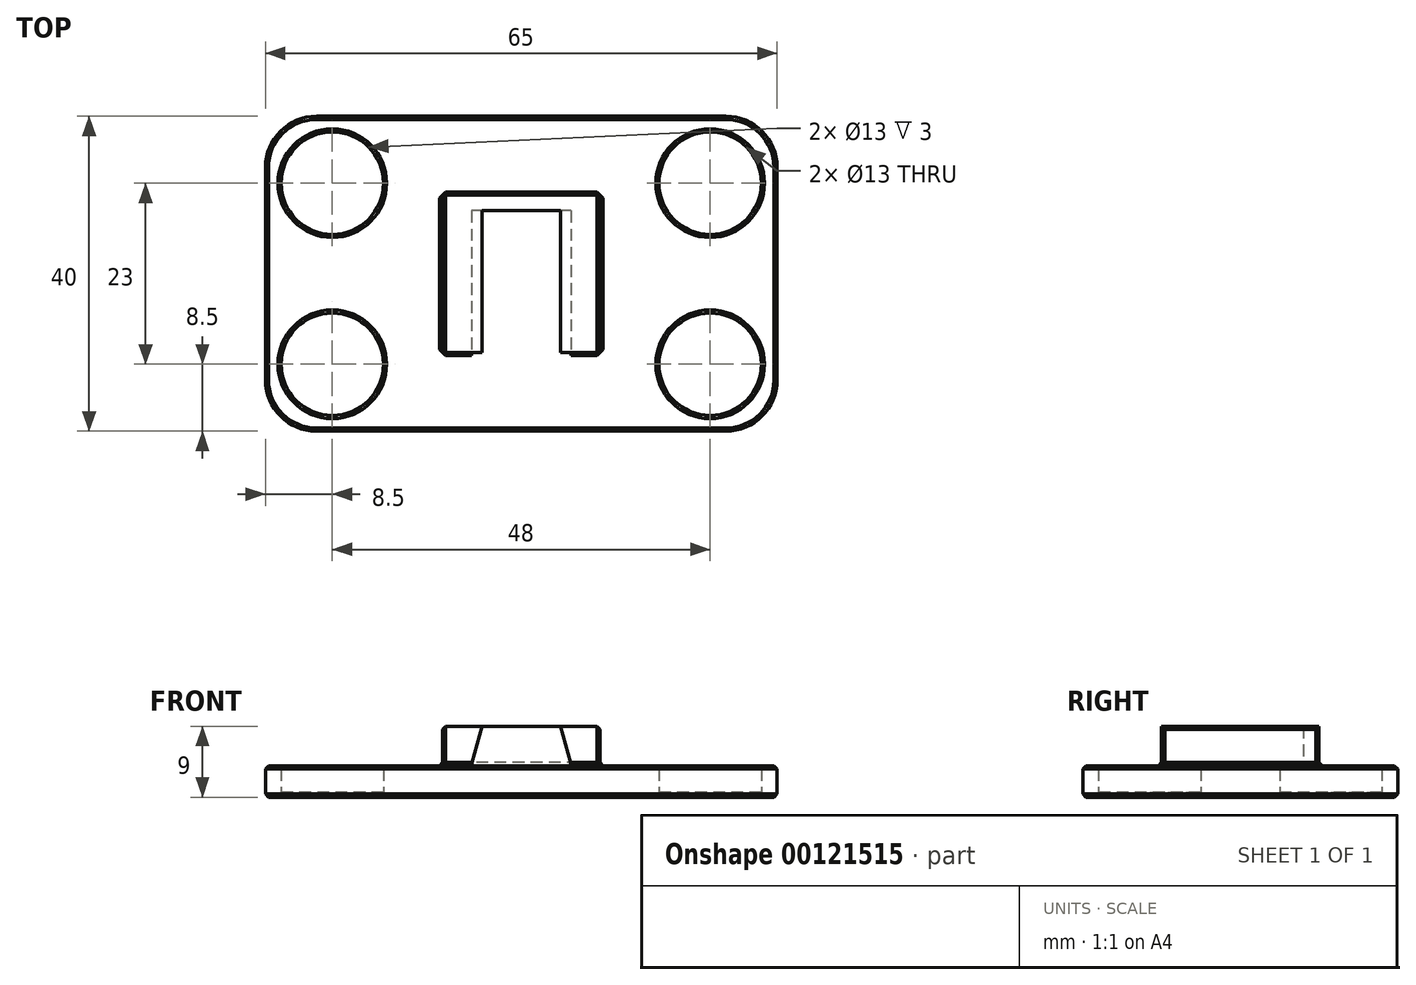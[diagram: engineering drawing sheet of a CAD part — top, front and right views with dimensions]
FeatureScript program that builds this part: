
annotation { "Feature Type Name" : "Feature", "Feature Type Description" : "" }
export const myFeature = defineFeature(function(context is Context, id is Id, definition is map)
    precondition{}
    {
        {
            assignVariable(context, id + "F0", {"name" : "PrintOffset", "anyValue" : 0.4});
        }
        {
            assignVariable(context, id + "F1", {"name" : "DovetailBackstopDepth", "anyValue" : 2});
        }
        {
            assignVariable(context, id + "F2", {"name" : "DovetailDepth", "anyValue" : 20});
        }
        {
            assignVariable(context, id + "F3", {"name" : "DovetailHeight", "anyValue" : 5});
        }
        {
            assignVariable(context, id + "F4", {"name" : "MagnetDiameter", "anyValue" : 13});
        }
        {
            assignVariable(context, id + "F5", {"name" : "WallThickness", "anyValue" : 4});
        }
        {
            var Q0;
            Q0=qCreatedBy(makeId("Top.planeOp"),FACE);
            var sketch = newSketch(context, id + "F6", { "sketchPlane" : qUnion([Q0])});
            skLineSegment(sketch, "E0", {"start": v(0, 0) * mm, "end": v(65, 0) * mm});
            skLineSegment(sketch, "E1", {"start": v(65, 0) * mm, "end": v(65, 40) * mm});
            skLineSegment(sketch, "E2", {"start": v(65, 40) * mm, "end": v(0, 40) * mm});
            skLineSegment(sketch, "E3", {"start": v(0, 40) * mm, "end": v(0, 0) * mm});
            skLineSegment(sketch, "E4", {"start": v(32.5, 40) * mm, "end": v(32.5, 0) * mm, "construction": true});
            skLineSegment(sketch, "E5", {"start": v(0, 20) * mm, "end": v(65, 20) * mm, "construction": true});
            skCircle(sketch, "E6", {"center": v(8.5, 31.5) * mm, "radius": 6.5 * mm});
            skCircle(sketch, "E7.MirrorC", {"center": v(56.5, 31.5) * mm, "radius": 6.5 * mm});
            skCircle(sketch, "E8.MirrorC", {"center": v(56.5, 8.5) * mm, "radius": 6.5 * mm});
            skCircle(sketch, "E9.MirrorC", {"center": v(8.5, 8.5) * mm, "radius": 6.5 * mm});
            skLineSegment(sketch, "E10.bottom", {"start": v(42.5, 30) * mm, "end": v(22.5, 30) * mm});
            skLineSegment(sketch, "E10.top", {"start": v(42.5, 10) * mm, "end": v(22.5, 10) * mm});
            skLineSegment(sketch, "E10.left", {"start": v(42.5, 30) * mm, "end": v(42.5, 10) * mm});
            skLineSegment(sketch, "E10.right", {"start": v(22.5, 30) * mm, "end": v(22.5, 10) * mm});
            skPoint(sketch, "E10.middle", {"position": v(32.5, 20) * mm});
            skLineSegment(sketch, "E11", {"start": v(22.5, 28) * mm, "end": v(42.5, 28) * mm});
            skSolve(sketch);
        }
        {
            var Q0;
            Q0=makeQuery(id+"F6.imprint","IMPRINT",FACE,{"disambiguationData":[TD([[makeQuery(id+"F6.imprint","IMPRINT",EDGE,{"derivedFrom":sQuery(id+"F6.wireOp",EDGE,"E0")}),1.0]])]});
            extrude(context, id + "F7", {"entities" : qUnion([Q0]), "depth" : (getVariable(context, 'WallThickness')) * mm});
        }
        {
            var Q0;
            Q0=makeQuery(id+"F6.imprint","IMPRINT",FACE,{"disambiguationData":[TD([[makeQuery(id+"F6.imprint","IMPRINT",EDGE,{"derivedFrom":sQuery(id+"F6.wireOp",EDGE,"E6")}),1.0]])]});
            var Q1;
            Q1=makeQuery(id+"F6.imprint","IMPRINT",FACE,{"disambiguationData":[TD([[makeQuery(id+"F6.imprint","IMPRINT",EDGE,{"derivedFrom":sQuery(id+"F6.wireOp",EDGE,"E9.MirrorC")}),-1.0]])]});
            var Q2;
            Q2=makeQuery(id+"F6.imprint","IMPRINT",FACE,{"disambiguationData":[TD([[makeQuery(id+"F6.imprint","IMPRINT",EDGE,{"derivedFrom":sQuery(id+"F6.wireOp",EDGE,"E8.MirrorC")}),1.0]])]});
            var Q3;
            Q3=makeQuery(id+"F6.imprint","IMPRINT",FACE,{"disambiguationData":[TD([[makeQuery(id+"F6.imprint","IMPRINT",EDGE,{"derivedFrom":sQuery(id+"F6.wireOp",EDGE,"E7.MirrorC")}),-1.0]])]});
            extrude(context, id + "F8", {"entities" : qUnion([Q0, Q1, Q2, Q3]), "operationType" : NewBodyOperationType.ADD, "depth" : .6 * mm});
        }
        {
            var Q0;
            {var subQ0=sQuery(id+"F6.wireOp",EDGE,"E10.top");Q0=makeQuery(id+"F6.imprint","IMPRINT",FACE,{"disambiguationData":[TD([[makeQuery(id+"F6.imprint","IMPRINT",EDGE,{"derivedFrom":subQ0}),-1.0]])]});}
            var Q1;
            {var subQ0=sQuery(id+"F6.wireOp",EDGE,"E10.bottom");Q1=makeQuery(id+"F6.imprint","IMPRINT",FACE,{"disambiguationData":[TD([[makeQuery(id+"F6.imprint","IMPRINT",EDGE,{"derivedFrom":subQ0}),1.0]])]});}
            extrude(context, id + "F9", {"entities" : qUnion([Q0, Q1]), "operationType" : NewBodyOperationType.ADD, "depth" : (getVariable(context, 'DovetailHeight') + getVariable(context, 'WallThickness')) * mm});
        }
        {
            var Q0;
            Q0=makeQuery(id+"F9.opExtrude","SWEPT_FACE",FACE,{"disambiguationData":[OSD([sQuery(id+"F6.wireOp",EDGE,"E10.top")])]});
            var sketch = newSketch(context, id + "F10", { "sketchPlane" : qUnion([Q0])});
            skLineSegment(sketch, "E12.0", {"start": v(42.5, 4) * mm, "end": v(22.5, 4) * mm});
            skLineSegment(sketch, "E12.1", {"start": v(22.5, 9) * mm, "end": v(22.5, 4) * mm});
            skLineSegment(sketch, "E12.2", {"start": v(42.5, 9) * mm, "end": v(22.5, 9) * mm});
            skLineSegment(sketch, "E12.3", {"start": v(42.5, 9) * mm, "end": v(42.5, 4) * mm});
            skLineSegment(sketch, "E13", {"start": v(27.5, 9) * mm, "end": v(26.16, 4) * mm});
            skLineSegment(sketch, "E14", {"start": v(32.5, 9) * mm, "end": v(32.5, 4) * mm, "construction": true});
            skLineSegment(sketch, "E15.MirrorCS", {"start": v(37.5, 9) * mm, "end": v(38.84, 4) * mm});
            skSolve(sketch);
        }
        {
            var Q0;
            {var subQ0=sQuery(id+"F10.wireOp",EDGE,"E13");Q0=makeQuery(id+"F10.imprint","IMPRINT",FACE,{"disambiguationData":[TD([[makeQuery(id+"F10.imprint","IMPRINT",EDGE,{"derivedFrom":subQ0}),1.0]])]});}
            extrude(context, id + "F11", {"entities" : qUnion([Q0]), "operationType" : NewBodyOperationType.REMOVE, "oppositeDirection" : true, "depth" : (getVariable(context, 'DovetailDepth') - getVariable(context, 'DovetailBackstopDepth')) * mm});
        }
        {
            var Q0;
            Q0=makeQuery(id+"F7.opExtrude","SWEPT_EDGE",EDGE,{"disambiguationData":[OSD([sQuery(id+"F6.wireOp",EDGE,"E0"),sQuery(id+"F6.wireOp",EDGE,"E3")])]});
            var Q1;
            Q1=makeQuery(id+"F7.opExtrude","SWEPT_EDGE",EDGE,{"disambiguationData":[OSD([sQuery(id+"F6.wireOp",EDGE,"E2"),sQuery(id+"F6.wireOp",EDGE,"E3")])]});
            var Q2;
            Q2=makeQuery(id+"F7.opExtrude","SWEPT_EDGE",EDGE,{"disambiguationData":[OSD([sQuery(id+"F6.wireOp",EDGE,"E0"),sQuery(id+"F6.wireOp",EDGE,"E1")])]});
            var Q3;
            Q3=makeQuery(id+"F7.opExtrude","SWEPT_EDGE",EDGE,{"disambiguationData":[OSD([sQuery(id+"F6.wireOp",EDGE,"E1"),sQuery(id+"F6.wireOp",EDGE,"E2")])]});
            fillet(context, id + "F12", {"entities" : qUnion([Q0, Q1, Q2, Q3]), "radius" : (getVariable(context, 'MagnetDiameter') / 2) * mm, "allowEdgeOverflow" : false});
        }
        {
            var Q0;
            {var subQ0=sQuery(id+"F6.wireOp",EDGE,"E10.right");var subQ1=sQuery(id+"F6.wireOp",EDGE,"E10.left");var subQ2=sQuery(id+"F6.wireOp",EDGE,"E10.top");var subQ3=sQuery(id+"F6.wireOp",EDGE,"E10.bottom");var subQ4=sQuery(id+"F6.wireOp",EDGE,"E9.MirrorC");var subQ5=sQuery(id+"F6.wireOp",EDGE,"E8.MirrorC");var subQ6=sQuery(id+"F6.wireOp",EDGE,"E7.MirrorC");var subQ7=sQuery(id+"F6.wireOp",EDGE,"E6");Q0=makeQuery(id+"F9.boolean.opBoolean","MERGE",FACE,{"derivedFrom":[makeQuery(id+"F8.boolean.opBoolean","MERGE",FACE,{"derivedFrom":[makeQuery(id+"F7.opExtrude","CAP_FACE",FACE,{"disambiguationData":[OSD([sQuery(id+"F6.wireOp",EDGE,"E0"),sQuery(id+"F6.wireOp",EDGE,"E1"),sQuery(id+"F6.wireOp",EDGE,"E2"),sQuery(id+"F6.wireOp",EDGE,"E3"),subQ7,subQ6,subQ5,subQ4,subQ3,subQ2,subQ1,subQ0])],"isStart":true}),makeQuery(id+"F8.opExtrude","CAP_FACE",FACE,{"disambiguationData":[OSD([subQ7])],"isStart":true}),makeQuery(id+"F8.opExtrude","CAP_FACE",FACE,{"disambiguationData":[OSD([subQ6])],"isStart":true}),makeQuery(id+"F8.opExtrude","CAP_FACE",FACE,{"disambiguationData":[OSD([subQ5])],"isStart":true}),makeQuery(id+"F8.opExtrude","CAP_FACE",FACE,{"disambiguationData":[OSD([subQ4])],"isStart":true})]}),makeQuery(id+"F9.opExtrude","CAP_FACE",FACE,{"disambiguationData":[OSD([subQ3,subQ2,subQ1,subQ0])],"isStart":true})]});}
            var Q1;
            Q1=makeQuery(id+"F9.opExtrude","SWEPT_FACE",FACE,{"disambiguationData":[OSD([sQuery(id+"F6.wireOp",EDGE,"E10.right")])]});
            var Q2;
            Q2=makeQuery(id+"F9.opExtrude","SWEPT_FACE",FACE,{"disambiguationData":[OSD([sQuery(id+"F6.wireOp",EDGE,"E10.left")])]});
            var Q3;
            Q3=makeQuery(id+"F7.opExtrude","CAP_EDGE",EDGE,{"disambiguationData":[OSD([sQuery(id+"F6.wireOp",EDGE,"E8.MirrorC")])],"isStart":false});
            var Q4;
            Q4=makeQuery(id+"F7.opExtrude","CAP_EDGE",EDGE,{"disambiguationData":[OSD([sQuery(id+"F6.wireOp",EDGE,"E7.MirrorC")])],"isStart":false});
            var Q5;
            Q5=makeQuery(id+"F7.opExtrude","CAP_EDGE",EDGE,{"disambiguationData":[OSD([sQuery(id+"F6.wireOp",EDGE,"E9.MirrorC")])],"isStart":false});
            var Q6;
            Q6=makeQuery(id+"F7.opExtrude","CAP_EDGE",EDGE,{"disambiguationData":[OSD([sQuery(id+"F6.wireOp",EDGE,"E6")])],"isStart":false});
            var Q7;
            Q7=makeQuery(id+"F7.opExtrude","CAP_EDGE",EDGE,{"disambiguationData":[OSD([sQuery(id+"F6.wireOp",EDGE,"E0")])],"isStart":false});
            chamfer(context, id + "F13", {"entities" : qUnion([Q0, Q1, Q2, Q3, Q4, Q5, Q6, Q7]), "width" : (getVariable(context, 'PrintOffset')) * mm, "tangentPropagation" : true});
        }
    });
